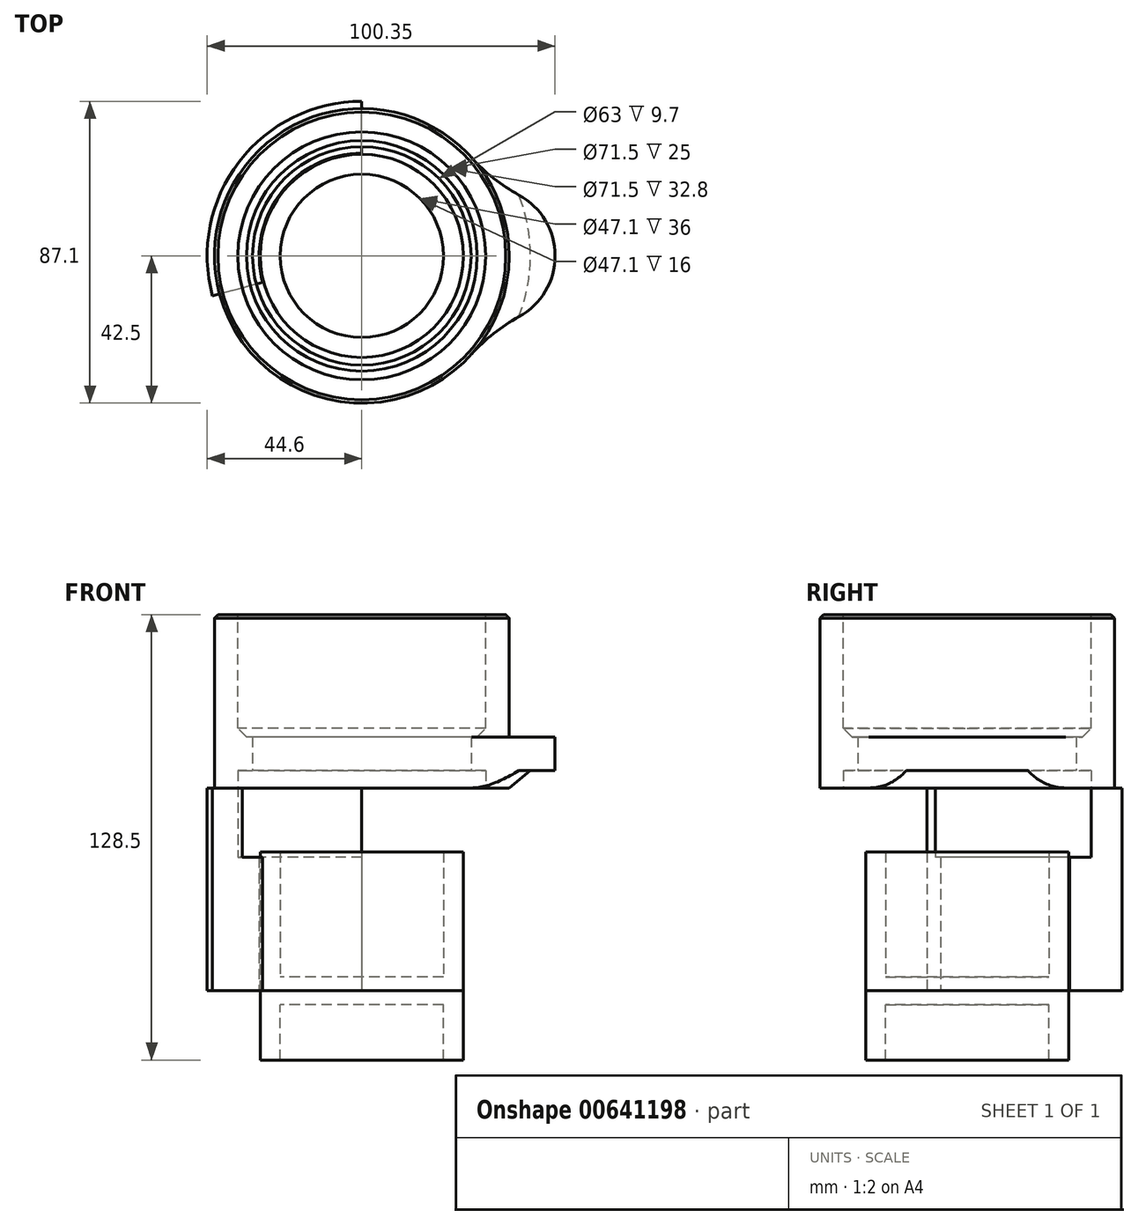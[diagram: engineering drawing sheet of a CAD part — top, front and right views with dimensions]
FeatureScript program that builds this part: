
annotation { "Feature Type Name" : "Feature", "Feature Type Description" : "" }
export const myFeature = defineFeature(function(context is Context, id is Id, definition is map)
    precondition{}
    {
        {
            var Q0;
            Q0=qCreatedBy(makeId("Top.planeOp"),FACE);
            var sketch = newSketch(context, id + "F0", { "sketchPlane" : qUnion([Q0])});
            skCircle(sketch, "E0", {"center": v(0, 0) * mm, "radius": 29.55 * mm});
            skSolve(sketch);
        }
        {
            var Q0;
            Q0=makeQuery(id+"F0.imprint","IMPRINT",FACE,{"disambiguationData":[TD([[makeQuery(id+"F0.imprint","IMPRINT",EDGE,{"derivedFrom":sQuery(id+"F0.wireOp",EDGE,"E0")}),1.0]])]});
            extrude(context, id + "F1", {"entities" : qUnion([Q0]), "depth" : 4 * mm, "offsetDistance" : 25 * mm});
        }
        {
            var Q0;
            Q0=makeQuery(id+"F1.opExtrude","CAP_FACE",FACE,{"disambiguationData":[OSD([sQuery(id+"F0.wireOp",EDGE,"E0")])],"isStart":false});
            var sketch = newSketch(context, id + "F2", { "sketchPlane" : qUnion([Q0])});
            skCircle(sketch, "E1", {"center": v(0, 0) * mm, "radius": 23.55 * mm});
            skSolve(sketch);
        }
        {
            var Q0;
            Q0=makeQuery(id+"F2.imprint","IMPRINT",FACE,{"disambiguationData":[TD([[makeQuery(id+"F2.imprint","IMPRINT",EDGE,{"derivedFrom":sQuery(id+"F2.wireOp",EDGE,"E1")}),-1.0]])]});
            extrude(context, id + "F3", {"entities" : qUnion([Q0]), "operationType" : NewBodyOperationType.ADD, "depth" : 36 * mm, "offsetDistance" : 25 * mm});
        }
        {
            var Q0;
            Q0=qCreatedBy(makeId("Top.planeOp"),FACE);
            var sketch = newSketch(context, id + "F4", { "sketchPlane" : qUnion([Q0])});
            skCircle(sketch, "E2", {"center": v(0, 0) * mm, "radius": 29.6 * mm});
            skCircle(sketch, "E3", {"center": v(0, 0) * mm, "radius": 44.6 * mm});
            skLineSegment(sketch, "E4", {"start": v(0, 0) * mm, "end": v(0, 44.6) * mm});
            skLineSegment(sketch, "E5.1.0", {"start": v(0, 0) * mm, "end": v(-38.62, -22.3) * mm});
            skLineSegment(sketch, "E5.2.0", {"start": v(0, 0) * mm, "end": v(38.62, -22.3) * mm});
            skLineSegment(sketch, "E6", {"start": v(0, 0) * mm, "end": v(11.54, 43.08) * mm});
            skLineSegment(sketch, "E7.1.0", {"start": v(0, 0) * mm, "end": v(-43.08, -11.54) * mm});
            skLineSegment(sketch, "E7.2.0", {"start": v(0, 0) * mm, "end": v(31.54, -31.54) * mm});
            skCircle(sketch, "E8", {"center": v(0, 0) * mm, "radius": 35.75 * mm});
            skSolve(sketch);
        }
        {
            var Q0;
            {var subQ0=sQuery(id+"F4.wireOp",EDGE,"E4");var subQ1=sQuery(id+"F4.wireOp",EDGE,"E2");var subQ2=makeQuery(id+"F4.imprint","INTERSECT",VERTEX,{"derivedFrom":[subQ1,subQ0]});Q0=makeQuery(id+"F4.imprint","IMPRINT",FACE,{"disambiguationData":[TD([[makeQuery(id+"F4.imprint","IMPRINT",EDGE,{"disambiguationData":[TD([[subQ2,-1.0]])],"derivedFrom":subQ1}),-1.0]])]});}
            extrude(context, id + "F5", {"entities" : qUnion([Q0]), "depth" : 38.5 * mm, "offsetDistance" : 25 * mm});
        }
        {
            var Q0;
            {var subQ0=sQuery(id+"F4.wireOp",EDGE,"E4");var subQ1=sQuery(id+"F4.wireOp",EDGE,"E3");var subQ2=makeQuery(id+"F4.imprint","INTERSECT",VERTEX,{"derivedFrom":[subQ1,subQ0]});Q0=makeQuery(id+"F4.imprint","IMPRINT",FACE,{"disambiguationData":[TD([[makeQuery(id+"F4.imprint","IMPRINT",EDGE,{"disambiguationData":[TD([[subQ2,-1.0]])],"derivedFrom":subQ1}),1.0]])]});}
            extrude(context, id + "F6", {"entities" : qUnion([Q0]), "operationType" : NewBodyOperationType.ADD, "depth" : (38.5 + 20) * mm, "offsetDistance" : 25 * mm});
        }
        {
            var Q0;
            Q0=makeQuery(id+"F3.opExtrude","CAP_FACE",FACE,{"disambiguationData":[OSD([sQuery(id+"F0.wireOp",EDGE,"E0"),sQuery(id+"F2.wireOp",EDGE,"E1")])],"isStart":false});
            var sketch = newSketch(context, id + "F7", { "sketchPlane" : qUnion([Q0])});
            skCircle(sketch, "E9", {"center": v(0, 0) * mm, "radius": 29.3 * mm});
            skSolve(sketch);
        }
        {
            var Q0;
            Q0=makeQuery(id+"F7.imprint","IMPRINT",FACE,{"disambiguationData":[TD([[makeQuery(id+"F7.imprint","IMPRINT",EDGE,{"derivedFrom":sQuery(id+"F7.wireOp",EDGE,"E9")}),-1.0]])]});
            var Q1;
            Q1=sQuery(id+"F4.wireOp",EDGE,"E5.2.0");
            var Q2;
            Q2=sQuery(id+"F7.wireOp",EDGE,"E9");
            var Q3;
            Q3=makeQuery(id+"F1.opExtrude","CAP_FACE",FACE,{"disambiguationData":[OSD([sQuery(id+"F0.wireOp",EDGE,"E0")])],"isStart":true});
            extrude(context, id + "F8", {"entities" : qUnion([Q0]), "operationType" : NewBodyOperationType.REMOVE, "surfaceEntities" : qUnion([Q1, Q2]), "endBound" : BoundingType.UP_TO_SURFACE, "oppositeDirection" : true, "depth" : 25 * mm, "endBoundEntityFace" : qUnion([Q3]), "offsetDistance" : 25 * mm});
        }
        {
            var Q0;
            Q0=makeQuery(id+"F6.opExtrude","CAP_FACE",FACE,{"disambiguationData":[OSD([sQuery(id+"F4.wireOp",EDGE,"E3"),sQuery(id+"F4.wireOp",EDGE,"E4"),sQuery(id+"F4.wireOp",EDGE,"E7.1.0"),sQuery(id+"F4.wireOp",EDGE,"E8")])],"isStart":false});
            var sketch = newSketch(context, id + "F9", { "sketchPlane" : qUnion([Q0])});
            skCircle(sketch, "E10", {"center": v(0, 0) * mm, "radius": 42.5 * mm});
            skCircle(sketch, "E11", {"center": v(0, 0) * mm, "radius": 35.75 * mm});
            skCircle(sketch, "E12", {"center": v(0, 0) * mm, "radius": 31.5 * mm});
            skSolve(sketch);
        }
        {
            var Q0;
            {var subQ0=sQuery(id+"F9.wireOp",EDGE,"E10");var subQ1=makeQuery(id+"F6.opExtrude","CAP_EDGE",EDGE,{"disambiguationData":[OSD([sQuery(id+"F4.wireOp",EDGE,"E4")])],"isStart":false});var subQ2=makeQuery(id+"F9.imprint","INTERSECT",VERTEX,{"derivedFrom":[subQ1,subQ0]});Q0=makeQuery(id+"F9.imprint","IMPRINT",FACE,{"disambiguationData":[TD([[makeQuery(id+"F9.imprint","IMPRINT",EDGE,{"disambiguationData":[TD([[subQ2,-1.0]])],"derivedFrom":subQ0}),1.0]])]});}
            var Q1;
            {var subQ0=sQuery(id+"F9.wireOp",EDGE,"E10");var subQ1=makeQuery(id+"F6.opExtrude","CAP_EDGE",EDGE,{"disambiguationData":[OSD([sQuery(id+"F4.wireOp",EDGE,"E4")])],"isStart":false});var subQ2=makeQuery(id+"F9.imprint","INTERSECT",VERTEX,{"derivedFrom":[subQ1,subQ0]});Q1=makeQuery(id+"F9.imprint","IMPRINT",FACE,{"disambiguationData":[TD([[makeQuery(id+"F9.imprint","IMPRINT",EDGE,{"disambiguationData":[TD([[subQ2,1.0]])],"derivedFrom":subQ0}),1.0]])]});}
            extrude(context, id + "F10", {"entities" : qUnion([Q0, Q1]), "depth" : 50 * mm, "offsetDistance" : 25 * mm});
        }
        {
            var Q0;
            Q0=makeQuery(id+"F9.imprint","IMPRINT",FACE,{"disambiguationData":[TD([[makeQuery(id+"F9.imprint","IMPRINT",EDGE,{"derivedFrom":sQuery(id+"F9.wireOp",EDGE,"E12")}),-1.0]])]});
            var Q1;
            Q1=makeQuery(id+"F10.opExtrude","CAP_FACE",FACE,{"disambiguationData":[OSD([sQuery(id+"F9.wireOp",EDGE,"E10"),sQuery(id+"F9.wireOp",EDGE,"E11")])],"isStart":false});
            extrude(context, id + "F11", {"entities" : qUnion([Q0]), "operationType" : NewBodyOperationType.ADD, "endBound" : BoundingType.UP_TO_SURFACE, "depth" : 25 * mm, "endBoundEntityFace" : qUnion([Q1]), "offsetDistance" : 25 * mm});
        }
        {
            var Q0;
            Q0=makeQuery(id+"F9.imprint","IMPRINT",FACE,{"disambiguationData":[TD([[makeQuery(id+"F9.imprint","IMPRINT",EDGE,{"derivedFrom":sQuery(id+"F9.wireOp",EDGE,"E12")}),-1.0]])]});
            extrude(context, id + "F12", {"entities" : qUnion([Q0]), "operationType" : NewBodyOperationType.REMOVE, "depth" : 5 * mm, "offsetDistance" : 25 * mm});
        }
        {
            var Q0;
            {var subQ0=sQuery(id+"F9.wireOp",EDGE,"E11");var subQ1=sQuery(id+"F9.wireOp",EDGE,"E10");Q0=makeQuery(id+"F11.boolean.opBoolean","MERGE",FACE,{"derivedFrom":[makeQuery(id+"F10.opExtrude","CAP_FACE",FACE,{"disambiguationData":[OSD([subQ1,subQ0])],"isStart":false}),makeQuery(id+"F11.opExtrude","CAP_FACE",FACE,{"disambiguationData":[OSD([subQ1,subQ0])],"isStart":false})]});}
            var sketch = newSketch(context, id + "F13", { "sketchPlane" : qUnion([Q0])});
            skCircle(sketch, "E13", {"center": v(0, 0) * mm, "radius": 35.75 * mm});
            skSolve(sketch);
        }
        {
            var Q0;
            Q0=makeQuery(id+"F13.imprint","IMPRINT",FACE,{"disambiguationData":[TD([[makeQuery(id+"F13.imprint","IMPRINT",EDGE,{"derivedFrom":sQuery(id+"F13.wireOp",EDGE,"E13")}),1.0]])]});
            extrude(context, id + "F14", {"entities" : qUnion([Q0]), "operationType" : NewBodyOperationType.REMOVE, "oppositeDirection" : true, "depth" : 35.3 * mm, "offsetDistance" : 25 * mm});
        }
        {
            var Q0;
            Q0=makeQuery(id+"F10.opExtrude","CAP_EDGE",EDGE,{"disambiguationData":[OSD([sQuery(id+"F9.wireOp",EDGE,"E10")])],"isStart":false});
            var Q1;
            Q1=makeQuery(id+"F14.boolean.opBoolean","COPY",EDGE,{"derivedFrom":makeQuery(id+"F14.opExtrude","CAP_EDGE",EDGE,{"disambiguationData":[OSD([sQuery(id+"F13.wireOp",EDGE,"E13")])],"isStart":true})});
            var Q2;
            Q2=makeQuery(id+"F14.boolean.opBoolean","COPY",EDGE,{"derivedFrom":makeQuery(id+"F14.opExtrude","CAP_EDGE",EDGE,{"disambiguationData":[OSD([sQuery(id+"F9.wireOp",EDGE,"E10"),sQuery(id+"F9.wireOp",EDGE,"E11"),sQuery(id+"F9.wireOp",EDGE,"E12")])],"isStart":false})});
            chamfer(context, id + "F15", {"entities" : qUnion([Q0, Q1, Q2]), "width" : 1 * mm, "tangentPropagation" : true});
        }
        {
            var Q0;
            Q0=makeQuery(id+"F1.opExtrude","SWEPT_BODY",BODY,{"disambiguationData":[OSD([sQuery(id+"F0.wireOp",EDGE,"E0")])]});
            var Q1;
            {var subQ0=sQuery(id+"F4.wireOp",EDGE,"E6");var subQ1=sQuery(id+"F4.wireOp",EDGE,"E2");var subQ2=makeQuery(id+"F4.imprint","INTERSECT",VERTEX,{"derivedFrom":[subQ1,subQ0]});Q1=makeQuery(id+"F4.imprint","IMPRINT",FACE,{"disambiguationData":[TD([[makeQuery(id+"F4.imprint","IMPRINT",EDGE,{"disambiguationData":[TD([[subQ2,1.0]])],"derivedFrom":subQ1}),1.0]])]});}
            mirror(context, id + "F16", {"entities" : qUnion([Q0]), "mirrorPlane" : qUnion([Q1])});
        }
        {
            var Q0;
            Q0=makeQuery(id+"F16.opPattern","COPY",FACE,{"derivedFrom":makeQuery(id+"F3.opExtrude","CAP_FACE",FACE,{"disambiguationData":[OSD([sQuery(id+"F0.wireOp",EDGE,"E0"),sQuery(id+"F2.wireOp",EDGE,"E1")])],"isStart":false}),"instanceName":"1"});
            extrude(context, id + "F17", {"entities" : qUnion([Q0]), "operationType" : NewBodyOperationType.REMOVE, "oppositeDirection" : true, "depth" : 20 * mm, "offsetDistance" : 25 * mm});
        }
        {
            var Q0;
            Q0=makeQuery(id+"F14.boolean.opBoolean","COPY",EDGE,{"derivedFrom":makeQuery(id+"F14.opExtrude","CAP_EDGE",EDGE,{"disambiguationData":[OSD([sQuery(id+"F13.wireOp",EDGE,"E13")])],"isStart":false})});
            chamfer(context, id + "F18", {"entities" : qUnion([Q0]), "width" : 2.5 * mm, "tangentPropagation" : true});
        }
        {
            var Q0;
            Q0=makeQuery(id+"F12.boolean.opBoolean","COPY",FACE,{"derivedFrom":makeQuery(id+"F12.opExtrude","CAP_FACE",FACE,{"disambiguationData":[OSD([sQuery(id+"F9.wireOp",EDGE,"E11"),sQuery(id+"F9.wireOp",EDGE,"E12")])],"isStart":false})});
            var sketch = newSketch(context, id + "F19", { "sketchPlane" : qUnion([Q0])});
            skLineSegment(sketch, "E14", {"start": v(0, 0) * mm, "end": v(-35.75, 0) * mm, "construction": true});
            skCircle(sketch, "E15", {"center": v(-35.75, 0) * mm, "radius": 20 * mm});
            skCircle(sketch, "E16.1.0", {"center": v(35.75, 0) * mm, "radius": 20 * mm});
            skPoint(sketch, "E16.center", {"position": v(0, 0) * mm});
            skSolve(sketch);
        }
        {
            var Q0;
            {var subQ0=sQuery(id+"F19.wireOp",EDGE,"E15");var subQ1=makeQuery(id+"F12.boolean.opBoolean","COPY",EDGE,{"derivedFrom":makeQuery(id+"F12.opExtrude","CAP_EDGE",EDGE,{"disambiguationData":[OSD([sQuery(id+"F9.wireOp",EDGE,"E11")])],"isStart":false})});var subQ2=makeQuery(id+"F19.imprint","INTERSECT",VERTEX,{"disambiguationData":[OD(0.0)],"derivedFrom":[subQ1,subQ0]});Q0=makeQuery(id+"F19.imprint","IMPRINT",FACE,{"disambiguationData":[TD([[makeQuery(id+"F19.imprint","IMPRINT",EDGE,{"disambiguationData":[TD([[subQ2,-1.0]])],"derivedFrom":subQ0}),1.0]])]});}
            var Q1;
            {var subQ0=sQuery(id+"F19.wireOp",EDGE,"E16.1.0");var subQ1=makeQuery(id+"F12.boolean.opBoolean","COPY",EDGE,{"derivedFrom":makeQuery(id+"F12.opExtrude","CAP_EDGE",EDGE,{"disambiguationData":[OSD([sQuery(id+"F9.wireOp",EDGE,"E11")])],"isStart":false})});var subQ2=makeQuery(id+"F19.imprint","INTERSECT",VERTEX,{"disambiguationData":[OD(0.0)],"derivedFrom":[subQ1,subQ0]});Q1=makeQuery(id+"F19.imprint","IMPRINT",FACE,{"disambiguationData":[TD([[makeQuery(id+"F19.imprint","IMPRINT",EDGE,{"disambiguationData":[TD([[subQ2,-1.0]])],"derivedFrom":subQ0}),1.0]])]});}
            var Q2;
            Q2=makeQuery(id+"F14.boolean.opBoolean","COPY",FACE,{"derivedFrom":makeQuery(id+"F14.opExtrude","CAP_FACE",FACE,{"disambiguationData":[OSD([sQuery(id+"F9.wireOp",EDGE,"E10"),sQuery(id+"F9.wireOp",EDGE,"E11"),sQuery(id+"F9.wireOp",EDGE,"E12"),sQuery(id+"F13.wireOp",EDGE,"E13")])],"isStart":false})});
            extrude(context, id + "F20", {"entities" : qUnion([Q0, Q1]), "operationType" : NewBodyOperationType.ADD, "endBound" : BoundingType.UP_TO_SURFACE, "oppositeDirection" : true, "depth" : 25 * mm, "endBoundEntityFace" : qUnion([Q2]), "offsetDistance" : 25 * mm});
        }
        {
            var Q0;
            Q0=makeQuery(id+"F20.boolean.opBoolean","INTERSECT",EDGE,{"disambiguationData":[OD(1.0)],"derivedFrom":[makeQuery(id+"F10.opExtrude","SWEPT_FACE",FACE,{"disambiguationData":[OSD([sQuery(id+"F9.wireOp",EDGE,"E10")])]}),makeQuery(id+"F20.opExtrude","SWEPT_FACE",FACE,{"disambiguationData":[OSD([sQuery(id+"F19.wireOp",EDGE,"E15")])]})]});
            var Q1;
            Q1=makeQuery(id+"F20.boolean.opBoolean","INTERSECT",EDGE,{"disambiguationData":[OD(0.0)],"derivedFrom":[makeQuery(id+"F10.opExtrude","SWEPT_FACE",FACE,{"disambiguationData":[OSD([sQuery(id+"F9.wireOp",EDGE,"E10")])]}),makeQuery(id+"F20.opExtrude","SWEPT_FACE",FACE,{"disambiguationData":[OSD([sQuery(id+"F19.wireOp",EDGE,"E15")])]})]});
            var Q2;
            Q2=makeQuery(id+"F20.boolean.opBoolean","INTERSECT",EDGE,{"disambiguationData":[OD(0.0)],"derivedFrom":[makeQuery(id+"F10.opExtrude","SWEPT_FACE",FACE,{"disambiguationData":[OSD([sQuery(id+"F9.wireOp",EDGE,"E10")])]}),makeQuery(id+"F20.opExtrude","SWEPT_FACE",FACE,{"disambiguationData":[OSD([sQuery(id+"F19.wireOp",EDGE,"E16.1.0")])]})]});
            var Q3;
            Q3=makeQuery(id+"F20.boolean.opBoolean","INTERSECT",EDGE,{"disambiguationData":[OD(1.0)],"derivedFrom":[makeQuery(id+"F10.opExtrude","SWEPT_FACE",FACE,{"disambiguationData":[OSD([sQuery(id+"F9.wireOp",EDGE,"E10")])]}),makeQuery(id+"F20.opExtrude","SWEPT_FACE",FACE,{"disambiguationData":[OSD([sQuery(id+"F19.wireOp",EDGE,"E16.1.0")])]})]});
            fillet(context, id + "F21", {"entities" : qUnion([Q0, Q1, Q2, Q3]), "radius" : 51.33 * mm, "tangentPropagation" : true, "allowEdgeOverflow" : false});
        }
        {
            var Q0;
            Q0=makeQuery(id+"F20.boolean.opBoolean","INTERSECT",EDGE,{"derivedFrom":[makeQuery(id+"F10.opExtrude","SWEPT_FACE",FACE,{"disambiguationData":[OSD([sQuery(id+"F9.wireOp",EDGE,"E10")])]}),makeQuery(id+"F20.opExtrude","CAP_FACE",FACE,{"disambiguationData":[OSD([sQuery(id+"F9.wireOp",EDGE,"E11"),sQuery(id+"F19.wireOp",EDGE,"E15")])],"isStart":true})]});
            var Q1;
            Q1=makeQuery(id+"F20.boolean.opBoolean","INTERSECT",EDGE,{"derivedFrom":[makeQuery(id+"F10.opExtrude","SWEPT_FACE",FACE,{"disambiguationData":[OSD([sQuery(id+"F9.wireOp",EDGE,"E10")])]}),makeQuery(id+"F20.opExtrude","CAP_FACE",FACE,{"disambiguationData":[OSD([sQuery(id+"F9.wireOp",EDGE,"E11"),sQuery(id+"F19.wireOp",EDGE,"E16.1.0")])],"isStart":true})]});
            chamfer(context, id + "F22", {"entities" : qUnion([Q0, Q1]), "chamferType" : ChamferType.TWO_OFFSETS, "width1" : 5 * mm, "oppositeDirection" : false, "width2" : 6.1 * mm, "tangentPropagation" : true});
        }
    });
